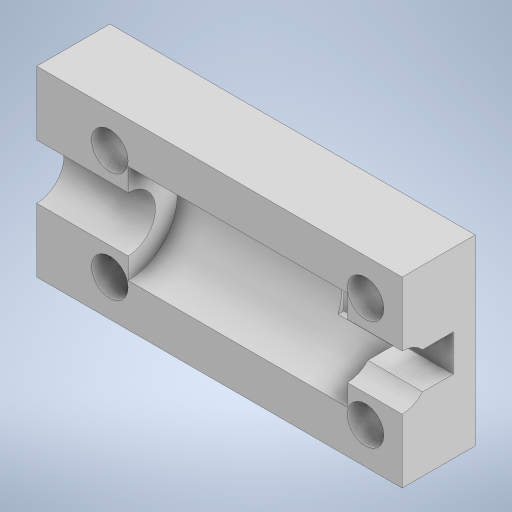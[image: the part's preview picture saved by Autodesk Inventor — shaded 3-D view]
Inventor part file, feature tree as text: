
AUTODESK INVENTOR PART (.ipt)
format: ipt  version: 2024 (Build 280153000, 153)  size: 385,536 bytes
history: native  units: mm
features: extrude x6, sketch x6, plane x4
ambient origin geometry x8: Origin, YZ Plane, XZ Plane, XY Plane, X Axis, Y Axis, Z Axis, Center Point
bodies: Solid1 (feature_tree)
feature tree (16):
  extrude  "Extrusion1"  Depth=10.0mm
  extrude  "Extrusion4"  Depth=3.0mm
  plane  "Work Plane2"
  extrude  "Extrusion6"  Depth=5.4mm TaperAngle=0.0deg
  plane  "Work Plane3"
  plane  "Work Plane4"
  plane  "Work Plane5"
  extrude  "Extrusion10"  Depth=2.0mm
  sketch  "Sketch1"  dims[d0=20.0mm d1=10.0mm]
  sketch  "Sketch5"  dims[d2=4.0mm d3=0.0mm d16=3.0mm]
  sketch  "Sketch7"  dims[d26=2.0mm d27=2.0mm]
  sketch  "Sketch12"  dims[d30=0.0mm d31=0.0mm d42=6.0mm d43=2.8mm d45=0.0mm d46=2.0mm d47=0.5mm d48=0.0mm d10=0.5mm d11=0.872665mm d12=0.5mm d13=0.872665mm]
  sketch  "Sketch6"  dims[d17=0.0mm d18=0.0mm d20=5.4mm d22=0.0mm d23=12.0mm]
  sketch  "Sketch10"  dims[d28=2.0mm d29=2.0mm]
  extrude  "Extrusion5"  Depth=2.0mm
  extrude  "Extrusion9"  Depth=6.0mm TaperAngle=0.0deg
